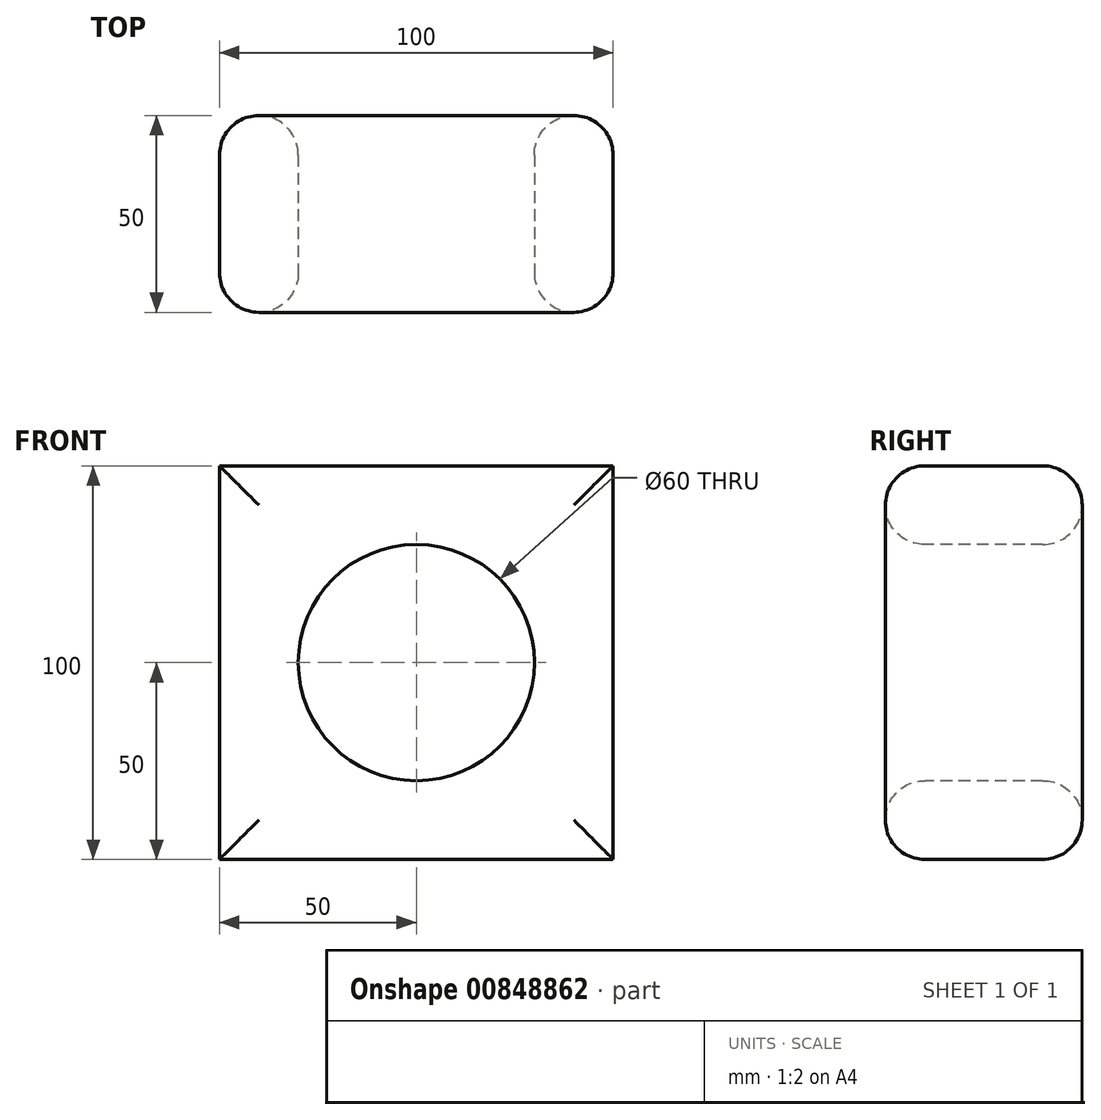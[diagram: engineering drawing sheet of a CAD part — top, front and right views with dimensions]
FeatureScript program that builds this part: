
annotation { "Feature Type Name" : "Feature", "Feature Type Description" : "" }
export const myFeature = defineFeature(function(context is Context, id is Id, definition is map)
    precondition{}
    {
        {
            var Q0;
            Q0=qCreatedBy(makeId("Front.planeOp"),FACE);
            var sketch = newSketch(context, id + "F0", { "sketchPlane" : qUnion([Q0])});
            skLineSegment(sketch, "E0.bottom", {"start": v(0, 0) * mm, "end": v(0, 0) * mm});
            skLineSegment(sketch, "E0.top", {"start": v(0, 0) * mm, "end": v(0, 0) * mm});
            skLineSegment(sketch, "E0.left", {"start": v(0, 0) * mm, "end": v(0, 0) * mm});
            skLineSegment(sketch, "E0.right", {"start": v(0, 0) * mm, "end": v(0, 0) * mm});
            skLineSegment(sketch, "E1.bottom", {"start": v(100, 0) * mm, "end": v(0, 0) * mm});
            skLineSegment(sketch, "E1.top", {"start": v(100, 100) * mm, "end": v(0, 100) * mm});
            skLineSegment(sketch, "E1.left", {"start": v(100, 0) * mm, "end": v(100, 100) * mm});
            skLineSegment(sketch, "E1.right", {"start": v(0, 0) * mm, "end": v(0, 100) * mm});
            skSolve(sketch);
        }
        {
            var Q0;
            Q0 = qSketchRegion(id + "F0", true);
            extrude(context, id + "F1", {"entities" : qUnion([Q0]), "depth" : 50 * mm, "offsetDistance" : 25 * mm});
        }
        {
            var Q0;
            Q0=makeQuery(id+"F1.opExtrude","CAP_FACE",FACE,{"disambiguationData":[OSD([sQuery(id+"F0.wireOp",EDGE,"E1.bottom"),sQuery(id+"F0.wireOp",EDGE,"E1.top"),sQuery(id+"F0.wireOp",EDGE,"E1.left"),sQuery(id+"F0.wireOp",EDGE,"E1.right")])],"isStart":false});
            var sketch = newSketch(context, id + "F2", { "sketchPlane" : qUnion([Q0])});
            skCircle(sketch, "E2", {"center": v(50, 50) * mm, "radius": 30 * mm});
            skSolve(sketch);
        }
        {
            var Q0;
            Q0=sQuery(id+"F2.wireOp",VERTEX,"E2.center");
            var Q1;
            Q1=makeQuery(id+"F1.opExtrude","SWEPT_BODY",BODY,{"disambiguationData":[OSD([sQuery(id+"F0.wireOp",EDGE,"E1.bottom"),sQuery(id+"F0.wireOp",EDGE,"E1.top"),sQuery(id+"F0.wireOp",EDGE,"E1.left"),sQuery(id+"F0.wireOp",EDGE,"E1.right")])]});
            hole(context, id + "F3", {"style" : HoleStyle.SIMPLE, "endStyle" : HoleEndStyle.THROUGH, "holeDiameter" : 60 * mm, "majorDiameter" : 5 * mm, "isTappedThrough" : true, "tappedDepth" : 12 * mm, "tapClearance" : 3, "locations" : qUnion([Q0]), "scope" : qUnion([Q1])});
        }
        {
            var Q0;
            Q0=makeQuery(id+"F1.opExtrude","CAP_FACE",FACE,{"disambiguationData":[OSD([sQuery(id+"F0.wireOp",EDGE,"E1.bottom"),sQuery(id+"F0.wireOp",EDGE,"E1.top"),sQuery(id+"F0.wireOp",EDGE,"E1.left"),sQuery(id+"F0.wireOp",EDGE,"E1.right")])],"isStart":false});
            var Q1;
            Q1=makeQuery(id+"F1.opExtrude","CAP_FACE",FACE,{"disambiguationData":[OSD([sQuery(id+"F0.wireOp",EDGE,"E1.bottom"),sQuery(id+"F0.wireOp",EDGE,"E1.top"),sQuery(id+"F0.wireOp",EDGE,"E1.left"),sQuery(id+"F0.wireOp",EDGE,"E1.right")])],"isStart":true});
            fillet(context, id + "F4", {"entities" : qUnion([Q0, Q1]), "radius" : 10 * mm, "tangentPropagation" : true, "allowEdgeOverflow" : false});
        }
    });
